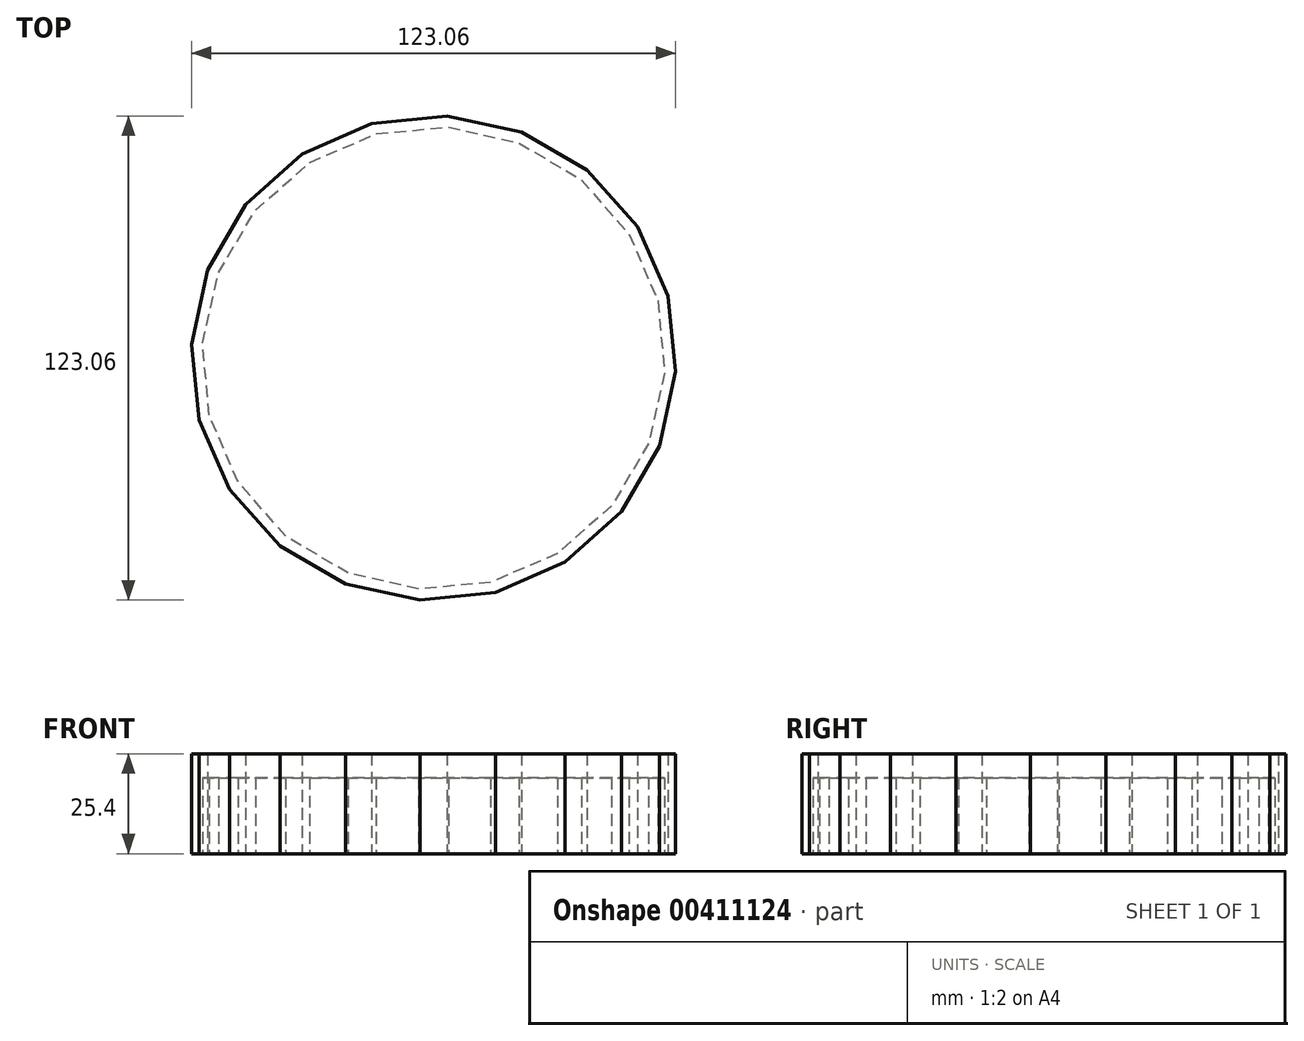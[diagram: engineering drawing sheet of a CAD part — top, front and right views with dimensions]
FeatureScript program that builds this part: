
annotation { "Feature Type Name" : "Feature", "Feature Type Description" : "" }
export const myFeature = defineFeature(function(context is Context, id is Id, definition is map)
    precondition{}
    {
        {
            var Q0;
            Q0=qCreatedBy(makeId("Top.planeOp"),FACE);
            var sketch = newSketch(context, id + "F0", { "sketchPlane" : qUnion([Q0])});
            skCircle(sketch, "E0.cCircle", {"center": v(0, 0) * mm, "radius": 60.86 * mm, "construction": true});
            skLineSegment(sketch, "E0.0", {"start": v(-57.44, 22.32) * mm, "end": v(-47.73, 38.98) * mm});
            skLineSegment(sketch, "E0.1", {"start": v(-47.73, 38.98) * mm, "end": v(-33.35, 51.82) * mm});
            skLineSegment(sketch, "E0.2", {"start": v(-33.35, 51.82) * mm, "end": v(-15.7, 59.59) * mm});
            skLineSegment(sketch, "E0.3", {"start": v(-15.7, 59.59) * mm, "end": v(3.48, 61.53) * mm});
            skLineSegment(sketch, "E0.4", {"start": v(3.48, 61.53) * mm, "end": v(22.32, 57.44) * mm});
            skLineSegment(sketch, "E0.5", {"start": v(22.32, 57.44) * mm, "end": v(38.98, 47.73) * mm});
            skLineSegment(sketch, "E0.6", {"start": v(38.98, 47.73) * mm, "end": v(51.82, 33.35) * mm});
            skLineSegment(sketch, "E0.7", {"start": v(51.82, 33.35) * mm, "end": v(59.59, 15.7) * mm});
            skLineSegment(sketch, "E0.8", {"start": v(59.59, 15.7) * mm, "end": v(61.53, -3.48) * mm});
            skLineSegment(sketch, "E0.9", {"start": v(61.53, -3.48) * mm, "end": v(57.44, -22.32) * mm});
            skLineSegment(sketch, "E0.10", {"start": v(57.44, -22.32) * mm, "end": v(47.73, -38.98) * mm});
            skLineSegment(sketch, "E0.11", {"start": v(47.73, -38.98) * mm, "end": v(33.35, -51.82) * mm});
            skLineSegment(sketch, "E0.12", {"start": v(33.35, -51.82) * mm, "end": v(15.7, -59.59) * mm});
            skLineSegment(sketch, "E0.13", {"start": v(15.7, -59.59) * mm, "end": v(-3.48, -61.53) * mm});
            skLineSegment(sketch, "E0.14", {"start": v(-3.48, -61.53) * mm, "end": v(-22.32, -57.44) * mm});
            skLineSegment(sketch, "E0.15", {"start": v(-22.32, -57.44) * mm, "end": v(-38.98, -47.73) * mm});
            skLineSegment(sketch, "E0.16", {"start": v(-38.98, -47.73) * mm, "end": v(-51.82, -33.35) * mm});
            skLineSegment(sketch, "E0.17", {"start": v(-51.82, -33.35) * mm, "end": v(-59.59, -15.7) * mm});
            skLineSegment(sketch, "E0.18", {"start": v(-59.59, -15.7) * mm, "end": v(-61.53, 3.48) * mm});
            skLineSegment(sketch, "E0.19", {"start": v(-61.53, 3.48) * mm, "end": v(-57.44, 22.32) * mm});
            skPoint(sketch, "E0.0.midPoint", {"position": v(-52.59, 30.65) * mm});
            skSolve(sketch);
        }
        {
            var Q0;
            Q0 = qSketchRegion(id + "F0", true);
            extrude(context, id + "F1", {"entities" : qUnion([Q0]), "depth" : 25.4 * mm});
        }
        {
            var Q0;
            Q0=qCreatedBy(makeId("Top.planeOp"),FACE);
            var sketch = newSketch(context, id + "F2", { "sketchPlane" : qUnion([Q0])});
            skCircle(sketch, "E1.cCircle", {"center": v(0, 0) * mm, "radius": 58.08 * mm, "construction": true});
            skLineSegment(sketch, "E1.0", {"start": v(-54.64, 21.73) * mm, "end": v(-45.26, 37.55) * mm});
            skLineSegment(sketch, "E1.1", {"start": v(-45.26, 37.55) * mm, "end": v(-31.44, 49.7) * mm});
            skLineSegment(sketch, "E1.2", {"start": v(-31.44, 49.7) * mm, "end": v(-14.54, 56.98) * mm});
            skLineSegment(sketch, "E1.3", {"start": v(-14.54, 56.98) * mm, "end": v(3.78, 58.68) * mm});
            skLineSegment(sketch, "E1.4", {"start": v(3.78, 58.68) * mm, "end": v(21.73, 54.64) * mm});
            skLineSegment(sketch, "E1.5", {"start": v(21.73, 54.64) * mm, "end": v(37.55, 45.26) * mm});
            skLineSegment(sketch, "E1.6", {"start": v(37.55, 45.26) * mm, "end": v(49.7, 31.44) * mm});
            skLineSegment(sketch, "E1.7", {"start": v(49.7, 31.44) * mm, "end": v(56.98, 14.54) * mm});
            skLineSegment(sketch, "E1.8", {"start": v(56.98, 14.54) * mm, "end": v(58.68, -3.78) * mm});
            skLineSegment(sketch, "E1.9", {"start": v(58.68, -3.78) * mm, "end": v(54.64, -21.73) * mm});
            skLineSegment(sketch, "E1.10", {"start": v(54.64, -21.73) * mm, "end": v(45.26, -37.55) * mm});
            skLineSegment(sketch, "E1.11", {"start": v(45.26, -37.55) * mm, "end": v(31.44, -49.7) * mm});
            skLineSegment(sketch, "E1.12", {"start": v(31.44, -49.7) * mm, "end": v(14.54, -56.98) * mm});
            skLineSegment(sketch, "E1.13", {"start": v(14.54, -56.98) * mm, "end": v(-3.78, -58.68) * mm});
            skLineSegment(sketch, "E1.14", {"start": v(-3.78, -58.68) * mm, "end": v(-21.73, -54.64) * mm});
            skLineSegment(sketch, "E1.15", {"start": v(-21.73, -54.64) * mm, "end": v(-37.55, -45.26) * mm});
            skLineSegment(sketch, "E1.16", {"start": v(-37.55, -45.26) * mm, "end": v(-49.7, -31.44) * mm});
            skLineSegment(sketch, "E1.17", {"start": v(-49.7, -31.44) * mm, "end": v(-56.98, -14.54) * mm});
            skLineSegment(sketch, "E1.18", {"start": v(-56.98, -14.54) * mm, "end": v(-58.68, 3.78) * mm});
            skLineSegment(sketch, "E1.19", {"start": v(-58.68, 3.78) * mm, "end": v(-54.64, 21.73) * mm});
            skPoint(sketch, "E1.0.midPoint", {"position": v(-49.95, 29.64) * mm});
            skSolve(sketch);
        }
        {
            var Q0;
            Q0 = qSketchRegion(id + "F2", true);
            extrude(context, id + "F3", {"entities" : qUnion([Q0]), "operationType" : NewBodyOperationType.REMOVE, "depth" : 19.3 * mm});
        }
    });
